# Revit family: Cilindros autonomos de 150 a 240l FK-5-1-12_Aguilera Extincion
name_source: partatom
category: Equipos especializados
units: mm (PartAtom-declared; Revit-internal decimal feet)

## family parameters
Anfitrión = Suelo
Compartido = No
Corte con vacíos al cargar = No
Cota de conector redondo = Radio de uso
Número OmniClass = 23.65.20.14.24
Punto de cálculo de habitación = No
Siempre vertical = Sí
Tipo de pieza = Normal
Título OmniClass = Other Gas Storage Vessels

## types (2) — shared parameters
Descripción = Cilindro de alta presión, fabricads en acero aleado tratado térmicamente soldados (según Directiva Europea 84/525/CEE). Marcado π . Presión de trabajo de 25 bar, temperatura de servicio de -20ºC a +50ºC, pintados en color rojo (RAL 3002).
Equipada con:
• Válvula de descarga 2 1/2″ con solenoide incorporada. Certiﬁcada CE y VdS.
• Actuador Manual. Certiﬁcado CE y VdS.
• Manómetro con presostato. Certiﬁcado CE y VdS.
• Herrajes para ﬁjación a pared.
• Caperuza de protección para transporte.
Fabricante = Aguilera Extinción
Símbolo = Sí
Símbolo texto = Sí
URL = https://aguilera.es

## per-type parameters (varying)
| type | Aux_R | Diámetro | H | H1 | H2 | Hd | L1 | Modelo | R |
| Cilindro autónomo MH5112® (FK-5-1-12) - 150 l | 102 mm | 406 mm  [stored 1.33202 ft] | 1709 mm  [stored 5.60696 ft] | 320 mm  [stored 1.04987 ft] | 920 mm  [stored 3.01837 ft] | 1439 mm | 564 mm | AEX/FK150 | 203 mm  [stored 0.66601 ft] |
| Cilindro autónomo MH5112® (FK-5-1-12) - 240 l | 116 mm | 462 mm  [stored 1.51575 ft] | 2000 mm  [stored 6.56168 ft] | 390 mm  [stored 1.27953 ft] | 1120 mm  [stored 3.67454 ft] | 1730 mm  [stored 5.67585 ft] | 596 mm  [stored 1.95538 ft] | AEX/FK240 | 231 mm  [stored 0.757874 ft] |

note: [stored X ft] marks values corroborated as IEEE doubles in the binary element streams (Revit-internal decimal feet)
